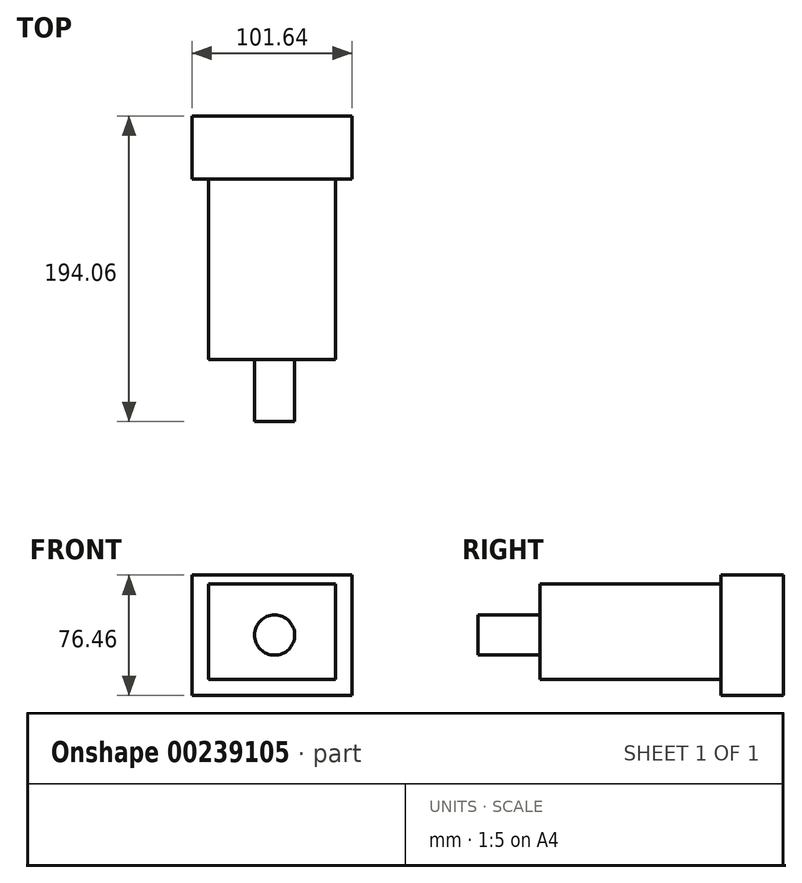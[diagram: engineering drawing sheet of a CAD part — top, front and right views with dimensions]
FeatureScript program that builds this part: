
annotation { "Feature Type Name" : "Feature", "Feature Type Description" : "" }
export const myFeature = defineFeature(function(context is Context, id is Id, definition is map)
    precondition{}
    {
        {
            var Q0;
            Q0=qCreatedBy(makeId("Front.planeOp"),FACE);
            var sketch = newSketch(context, id + "F0", { "sketchPlane" : qUnion([Q0])});
            skLineSegment(sketch, "E0.bottom", {"start": v(-52.49, 38.08) * mm, "end": v(49.15, 38.08) * mm});
            skLineSegment(sketch, "E0.top", {"start": v(-52.49, -38.38) * mm, "end": v(49.15, -38.38) * mm});
            skLineSegment(sketch, "E0.left", {"start": v(-52.49, 38.08) * mm, "end": v(-52.49, -38.38) * mm});
            skLineSegment(sketch, "E0.right", {"start": v(49.15, 38.08) * mm, "end": v(49.15, -38.38) * mm});
            skSolve(sketch);
        }
        {
            var Q0;
            Q0 = qSketchRegion(id + "F0", true);
            extrude(context, id + "F1", {"entities" : qUnion([Q0]), "depth" : 39.88 * mm});
        }
        {
            var Q0;
            Q0=makeQuery(id+"F1.opExtrude","CAP_FACE",FACE,{"disambiguationData":[OSD([sQuery(id+"F0.wireOp",EDGE,"E0.bottom"),sQuery(id+"F0.wireOp",EDGE,"E0.top"),sQuery(id+"F0.wireOp",EDGE,"E0.left"),sQuery(id+"F0.wireOp",EDGE,"E0.right")])],"isStart":false});
            var sketch = newSketch(context, id + "F2", { "sketchPlane" : qUnion([Q0])});
            skLineSegment(sketch, "E1.bottom", {"start": v(-41.9, -28.22) * mm, "end": v(38.57, -28.22) * mm});
            skLineSegment(sketch, "E1.top", {"start": v(-41.9, 32.5) * mm, "end": v(38.57, 32.5) * mm});
            skLineSegment(sketch, "E1.left", {"start": v(-41.9, -28.22) * mm, "end": v(-41.9, 32.5) * mm});
            skLineSegment(sketch, "E1.right", {"start": v(38.57, -28.22) * mm, "end": v(38.57, 32.5) * mm});
            skSolve(sketch);
        }
        {
            var Q0;
            Q0 = qSketchRegion(id + "F2", true);
            extrude(context, id + "F3", {"entities" : qUnion([Q0]), "operationType" : NewBodyOperationType.ADD, "depth" : 114.8 * mm});
        }
        {
            var Q0;
            Q0=makeQuery(id+"F3.opExtrude","CAP_FACE",FACE,{"disambiguationData":[OSD([sQuery(id+"F2.wireOp",EDGE,"E1.bottom"),sQuery(id+"F2.wireOp",EDGE,"E1.top"),sQuery(id+"F2.wireOp",EDGE,"E1.left"),sQuery(id+"F2.wireOp",EDGE,"E1.right")])],"isStart":false});
            var sketch = newSketch(context, id + "F4", { "sketchPlane" : qUnion([Q0])});
            skCircle(sketch, "E2", {"center": v(0, 0) * mm, "radius": 12.76 * mm});
            skSolve(sketch);
        }
        {
            var Q0;
            Q0 = qSketchRegion(id + "F4", true);
            extrude(context, id + "F5", {"entities" : qUnion([Q0]), "operationType" : NewBodyOperationType.ADD, "depth" : 39.37 * mm});
        }
        {
            var Q0;
            Q0=makeQuery(id+"F3.opExtrude","SWEPT_FACE",FACE,{"disambiguationData":[OSD([sQuery(id+"F2.wireOp",EDGE,"E1.top")])]});
            var sketch = newSketch(context, id + "F6", { "sketchPlane" : qUnion([Q0])});
            skLineSegment(sketch, "E3.bottom", {"start": v(25.78, -142.07) * mm, "end": v(-26.56, -142.07) * mm});
            skLineSegment(sketch, "E3.top", {"start": v(25.78, -49.93) * mm, "end": v(-26.56, -49.93) * mm});
            skLineSegment(sketch, "E3.left", {"start": v(25.78, -142.07) * mm, "end": v(25.78, -49.93) * mm});
            skLineSegment(sketch, "E3.right", {"start": v(-26.56, -142.07) * mm, "end": v(-26.56, -49.93) * mm});
            skSolve(sketch);
        }
        {
            var Q0;
            Q0 = qSketchRegion(id + "F6", true);
            extrude(context, id + "F7", {"entities" : qUnion([Q0]), "operationType" : NewBodyOperationType.ADD, "oppositeDirection" : true, "depth" : 27.94 * mm});
        }
    });
